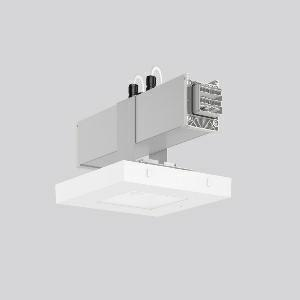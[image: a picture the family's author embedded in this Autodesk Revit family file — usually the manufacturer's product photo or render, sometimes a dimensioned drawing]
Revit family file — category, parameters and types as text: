
# Revit family: linedo_module_rf_9503rf_760_409_100_d0f1
name_source: partatom
category: Lighting Fixtures
units: mm (PartAtom-declared; Revit-internal decimal feet)

## family parameters
Cut with Voids When Loaded = No
Host = Face
Light Source = No
Part Type = Normal
Room Calculation Point = No
Round Connector Dimension = Use Diameter
Shared = No

## types (1)
- LINEDO Module RF (1 x LED Modul 765, 220 lm, 6500)
    Apparent Load = 4 VA
    CIE Flux Codes = 49 90 100 100 100
    Color Rendering = 70
    Color Temperature = 6500
    Default Elevation = 1800 mm
    Description = LINEDO, 4,2 W, 220 lm, 765, silver, on/off
Continuous line luminaire, L 330 B 198 H 170, CBS, emergency-220 lm, AC-Control
    Height = 170 mm  [stored 0.557743 ft]
    Lamp = 1 x LED Modul 765
    Lamp Light Flux = 220 lm
    Lamp count = 1
    Length = 330 mm
    Lifetime = 50000 h
    Luminous efficacy = 52 lm/W
    Manufacturer = RZB
    ModVariant = No
    Model = 9503RF.760.409.100
    Mounting Place = Ceiling
    Mounting Type = Surface mounted, Pendant
    Number of Poles = 1
    OnlyDefault = Yes
    Power Factor = 1
    Product Name = LINEDO Module RF
    Product group = Continuous line luminaire system Linedo IP 54
    ProductGroupID = 314
    Protection Class = Protection class I
    Protection Degree = IP 54
    RLX_Detail_Level = 1
    RLX_Emergency_Light_Flux = 220 lm
    RLX_Emergency_Type = 3
    RLX_Emergency_Type_DB = Yes
    RlxData = <blob elided: 29737 chars, md5=a651a88f>
    Socket = socket
    Standby Power = 0 W
    System Light Flux = 220 lm
    System Power = 4 W
    Type Comments = Product without accessories
    Type Image = 9503rw.760.434.000.jpg
    URL = http://relux.com
    VarID = ---
    Voltage = 230 V
    Voltage Range = 220-240 V
    Weight = 0.00 kg
    Width = 198 mm

note: [stored X ft] marks values corroborated as IEEE doubles in the binary element streams (Revit-internal decimal feet)

## geometry (parser evidence)
native form markers: Blend x4, Sweep x15
no freeform markers — native parametric forms only
